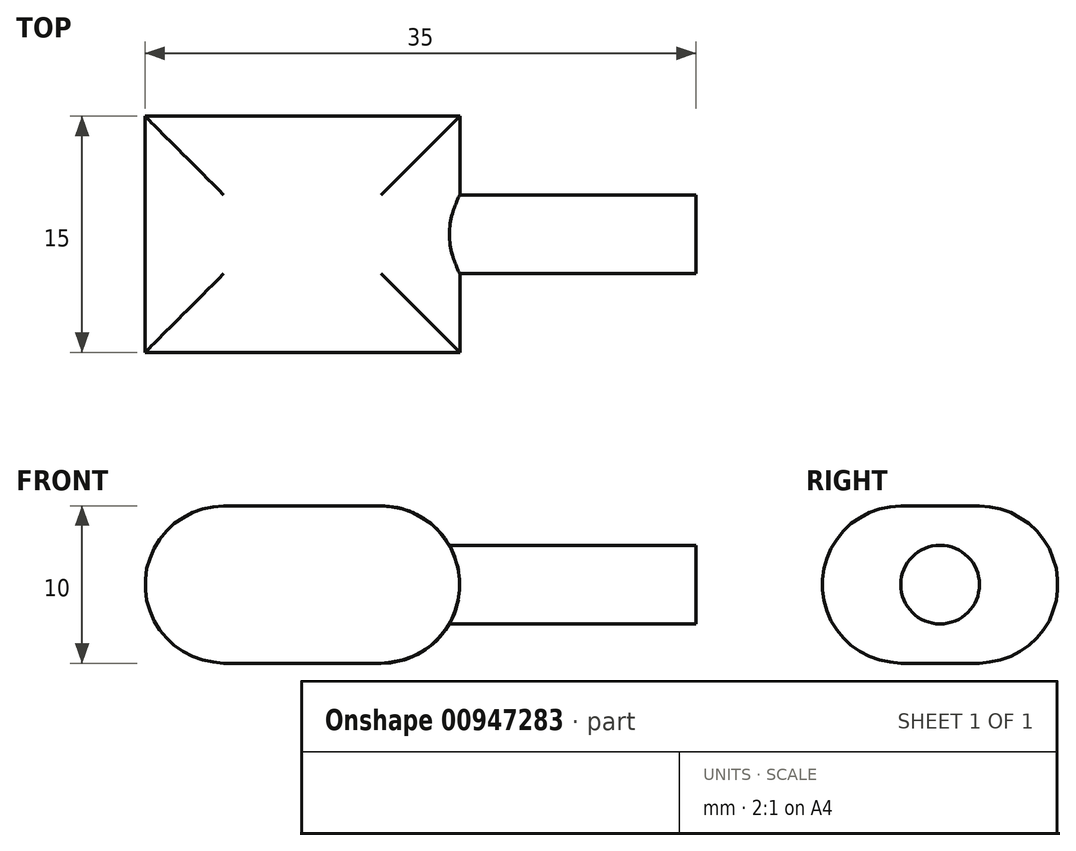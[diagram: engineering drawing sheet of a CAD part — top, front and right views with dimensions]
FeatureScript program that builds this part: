
annotation { "Feature Type Name" : "Feature", "Feature Type Description" : "" }
export const myFeature = defineFeature(function(context is Context, id is Id, definition is map)
    precondition{}
    {
        {
            var Q0;
            Q0=qCreatedBy(makeId("Top.planeOp"),FACE);
            var sketch = newSketch(context, id + "F0", { "sketchPlane" : qUnion([Q0])});
            skLineSegment(sketch, "E0.bottom", {"start": v(-10, -7.5) * mm, "end": v(10, -7.5) * mm});
            skLineSegment(sketch, "E0.top", {"start": v(-10, 7.5) * mm, "end": v(10, 7.5) * mm});
            skLineSegment(sketch, "E0.left", {"start": v(-10, -7.5) * mm, "end": v(-10, 7.5) * mm});
            skLineSegment(sketch, "E0.right", {"start": v(10, -7.5) * mm, "end": v(10, 7.5) * mm});
            skSolve(sketch);
        }
        {
            var Q0;
            Q0=makeQuery(id+"F0.imprint","IMPRINT",FACE,{"disambiguationData":[TD([[makeQuery(id+"F0.imprint","IMPRINT",EDGE,{"derivedFrom":sQuery(id+"F0.wireOp",EDGE,"E0.bottom")}),1.0]])]});
            extrude(context, id + "F1", {"entities" : qUnion([Q0]), "endBound" : BoundingType.SYMMETRIC, "depth" : 10 * mm, "offsetDistance" : 25 * mm});
        }
        {
            var Q0;
            Q0=makeQuery(id+"F1.opExtrude","CAP_EDGE",EDGE,{"disambiguationData":[OSD([sQuery(id+"F0.wireOp",EDGE,"E0.top")])],"isStart":false});
            var Q1;
            Q1=makeQuery(id+"F1.opExtrude","CAP_FACE",FACE,{"disambiguationData":[OSD([sQuery(id+"F0.wireOp",EDGE,"E0.bottom"),sQuery(id+"F0.wireOp",EDGE,"E0.top"),sQuery(id+"F0.wireOp",EDGE,"E0.left"),sQuery(id+"F0.wireOp",EDGE,"E0.right")])],"isStart":false});
            var Q2;
            Q2=makeQuery(id+"F1.opExtrude","CAP_EDGE",EDGE,{"disambiguationData":[OSD([sQuery(id+"F0.wireOp",EDGE,"E0.bottom")])],"isStart":true});
            var Q3;
            Q3=makeQuery(id+"F1.opExtrude","CAP_EDGE",EDGE,{"disambiguationData":[OSD([sQuery(id+"F0.wireOp",EDGE,"E0.right")])],"isStart":true});
            var Q4;
            Q4=makeQuery(id+"F1.opExtrude","CAP_EDGE",EDGE,{"disambiguationData":[OSD([sQuery(id+"F0.wireOp",EDGE,"E0.top")])],"isStart":true});
            var Q5;
            Q5=makeQuery(id+"F1.opExtrude","CAP_EDGE",EDGE,{"disambiguationData":[OSD([sQuery(id+"F0.wireOp",EDGE,"E0.left")])],"isStart":true});
            fillet(context, id + "F2", {"entities" : qUnion([Q0, Q1, Q2, Q3, Q4, Q5]), "tangentPropagation" : true, "radius" : 5 * mm, "defaultsChanged" : false, "vertexSettings" : [], "allowEdgeOverflow" : false});
        }
        {
            var Q0;
            Q0=qCreatedBy(makeId("Right.planeOp"),FACE);
            var sketch = newSketch(context, id + "F3", { "sketchPlane" : qUnion([Q0])});
            skCircle(sketch, "E1", {"center": v(0, 0) * mm, "radius": 2.5 * mm});
            skSolve(sketch);
        }
        {
            var Q0;
            Q0 = qSketchRegion(id + "F3", true);
            extrude(context, id + "F4", {"entities" : qUnion([Q0]), "operationType" : NewBodyOperationType.ADD, "depth" : 25 * mm, "offsetDistance" : 25 * mm});
        }
    });
